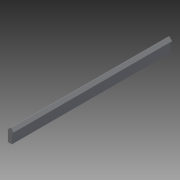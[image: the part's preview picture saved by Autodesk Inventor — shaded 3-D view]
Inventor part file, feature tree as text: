
AUTODESK INVENTOR PART (.ipt)
format: ipt  version: 2016 SP1 (Build 200210100, 210)  size: 99,840 bytes
history: native  units: in
note: dims shown in document units (in); Inventor stores cm internally (conversion verified against a paired STEP export)
features: fillet x1, other x1, imported_body x1
ambient origin geometry x8: Origin, YZ Plane, XZ Plane, XY Plane, X Axis, Y Axis, Z Axis, Center Point
bodies: Body1 (feature_tree)
feature tree (3):
  fillet  "Fillet1"  [1 undecoded]
  other  "BWC-T4-11"
  imported_body  "Base1"
note: 1 required parameter value undecoded (feature->parameter linkage not recoverable at this tier; creation-order binding heuristic only, values carry confidence <= 0.55)
